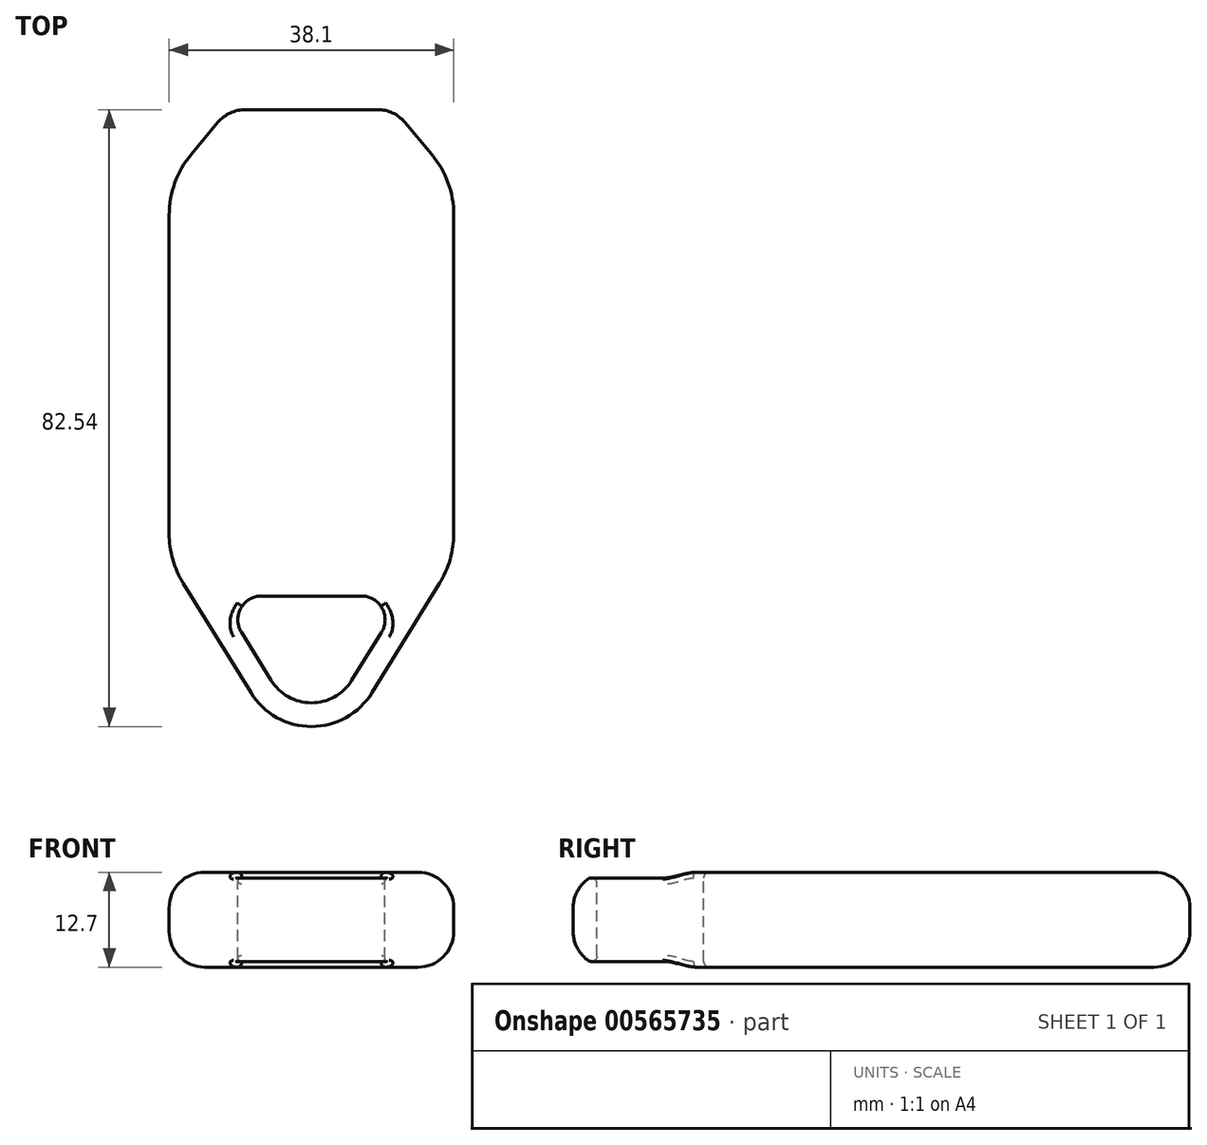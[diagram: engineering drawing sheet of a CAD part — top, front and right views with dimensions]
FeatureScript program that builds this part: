
annotation { "Feature Type Name" : "Feature", "Feature Type Description" : "" }
export const myFeature = defineFeature(function(context is Context, id is Id, definition is map)
    precondition{}
    {
        {
            var Q0;
            Q0=qCreatedBy(makeId("Top.planeOp"),FACE);
            var sketch = newSketch(context, id + "F0", { "sketchPlane" : qUnion([Q0])});
            skLineSegment(sketch, "E0.bottom", {"start": v(19.05, 25.4) * mm, "end": v(-19.05, 25.4) * mm});
            skLineSegment(sketch, "E0.top", {"start": v(19.05, -25.4) * mm, "end": v(-19.05, -25.4) * mm});
            skLineSegment(sketch, "E0.left", {"start": v(19.05, 25.4) * mm, "end": v(19.05, -25.4) * mm});
            skLineSegment(sketch, "E0.right", {"start": v(-19.05, 25.4) * mm, "end": v(-19.05, -25.4) * mm});
            skPoint(sketch, "E0.middle", {"position": v(0, 0) * mm});
            skSolve(sketch);
        }
        {
            var Q0;
            Q0=makeQuery(id+"F0.imprint","IMPRINT",FACE,{"disambiguationData":[TD([[makeQuery(id+"F0.imprint","IMPRINT",EDGE,{"derivedFrom":sQuery(id+"F0.wireOp",EDGE,"E0.bottom")}),1.0]])]});
            extrude(context, id + "F1", {"entities" : qUnion([Q0]), "depth" : 12.7 * mm, "offsetDistance" : 25.4 * mm, "symmetric" : true});
        }
        {
            var Q0;
            Q0=makeQuery(id+"F1.opExtrude","CAP_FACE",FACE,{"disambiguationData":[OSD([sQuery(id+"F0.wireOp",EDGE,"E0.bottom"),sQuery(id+"F0.wireOp",EDGE,"E0.top"),sQuery(id+"F0.wireOp",EDGE,"E0.left"),sQuery(id+"F0.wireOp",EDGE,"E0.right")])],"isStart":false});
            var sketch = newSketch(context, id + "F2", { "sketchPlane" : qUnion([Q0])});
            skLineSegment(sketch, "E1", {"start": v(0, 25.4) * mm, "end": v(0, 34.92) * mm, "construction": true});
            skPoint(sketch, "E1.endSnap0", {"position": v(0, 25.4) * mm});
            skLineSegment(sketch, "E2", {"start": v(-19.05, 25.4) * mm, "end": v(-12.5, 33.22) * mm});
            skLineSegment(sketch, "E3", {"start": v(-8.85, 34.92) * mm, "end": v(0, 34.92) * mm});
            skLineSegment(sketch, "E4.MirrorCS", {"start": v(19.05, 25.4) * mm, "end": v(12.5, 33.22) * mm});
            skLineSegment(sketch, "E5.MirrorCS", {"start": v(8.85, 34.92) * mm, "end": v(0, 34.92) * mm});
            skLineSegment(sketch, "E6", {"start": v(-19.05, 25.4) * mm, "end": v(19.05, 25.4) * mm});
            skLineSegment(sketch, "E7", {"start": v(0, -25.4) * mm, "end": v(0, -38.1) * mm, "construction": true});
            skPoint(sketch, "E7.endSnap0", {"position": v(0, -25.4) * mm});
            skArc(sketch, "E8", {"start": v(-8.1, -43.1) * mm, "mid": v(0, -47.62) * mm, "end": v(8.1, -43.1) * mm});
            skLineSegment(sketch, "E9", {"start": v(-19.05, -25.4) * mm, "end": v(-8.1, -43.1) * mm});
            skLineSegment(sketch, "E10", {"start": v(19.05, -25.4) * mm, "end": v(8.1, -43.1) * mm});
            skArc(sketch, "E11", {"start": v(-5.4, -41.44) * mm, "mid": v(0, -44.45) * mm, "end": v(5.4, -41.44) * mm});
            skLineSegment(sketch, "E12", {"start": v(-5.4, -41.44) * mm, "end": v(-9.38, -35) * mm});
            skLineSegment(sketch, "E13", {"start": v(-6.68, -30.16) * mm, "end": v(6.68, -30.16) * mm});
            skLineSegment(sketch, "E14", {"start": v(9.38, -35) * mm, "end": v(5.4, -41.44) * mm});
            skPoint(sketch, "E15.visualSharp", {"position": v(-12.37, -30.16) * mm});
            skArc(sketch, "E15.filletArc", {"start": v(-6.68, -30.16) * mm, "mid": v(-9.45, -31.8) * mm, "end": v(-9.38, -35) * mm});
            skPoint(sketch, "E16.visualSharp", {"position": v(12.37, -30.16) * mm});
            skArc(sketch, "E16.filletArc", {"start": v(9.38, -35) * mm, "mid": v(9.45, -31.8) * mm, "end": v(6.68, -30.16) * mm});
            skPoint(sketch, "E17.visualSharp", {"position": v(-11.07, 34.93) * mm});
            skArc(sketch, "E17.filletArc", {"start": v(-8.85, 34.93) * mm, "mid": v(-10.86, 34.48) * mm, "end": v(-12.5, 33.22) * mm});
            skPoint(sketch, "E18.visualSharp", {"position": v(11.07, 34.93) * mm});
            skArc(sketch, "E18.filletArc", {"start": v(12.5, 33.22) * mm, "mid": v(10.86, 34.48) * mm, "end": v(8.85, 34.93) * mm});
            skSolve(sketch);
        }
        {
            var Q0;
            Q0=makeQuery(id+"F2.imprint","IMPRINT",FACE,{"disambiguationData":[TD([[makeQuery(id+"F2.imprint","IMPRINT",EDGE,{"derivedFrom":sQuery(id+"F2.wireOp",EDGE,"E2")}),-1.0]])]});
            var Q1;
            Q1=makeQuery(id+"F2.imprint","IMPRINT",FACE,{"disambiguationData":[TD([[makeQuery(id+"F2.imprint","IMPRINT",EDGE,{"derivedFrom":sQuery(id+"F2.wireOp",EDGE,"E8")}),1.0]])]});
            var Q2;
            Q2=makeQuery(id+"F1.opExtrude","CAP_FACE",FACE,{"disambiguationData":[OSD([sQuery(id+"F0.wireOp",EDGE,"E0.bottom"),sQuery(id+"F0.wireOp",EDGE,"E0.top"),sQuery(id+"F0.wireOp",EDGE,"E0.left"),sQuery(id+"F0.wireOp",EDGE,"E0.right")])],"isStart":true});
            extrude(context, id + "F3", {"entities" : qUnion([Q0, Q1]), "operationType" : NewBodyOperationType.ADD, "endBound" : BoundingType.UP_TO_SURFACE, "oppositeDirection" : true, "depth" : 25.4 * mm, "endBoundEntityFace" : qUnion([Q2]), "offsetDistance" : 25.4 * mm});
        }
        {
            var Q0;
            {var subQ0=sQuery(id+"F0.wireOp",EDGE,"E0.right");Q0=makeQuery(id+"F3.boolean.opBoolean","MERGE",EDGE,{"derivedFrom":[makeQuery(id+"F1.opExtrude","SWEPT_EDGE",EDGE,{"disambiguationData":[OSD([sQuery(id+"F0.wireOp",EDGE,"E0.bottom"),subQ0])]}),makeQuery(id+"F3.opExtrude","SWEPT_EDGE",EDGE,{"disambiguationData":[OSD([subQ0,sQuery(id+"F2.wireOp",EDGE,"E2"),sQuery(id+"F2.wireOp",EDGE,"E6")])]})]});}
            var Q1;
            {var subQ0=sQuery(id+"F0.wireOp",EDGE,"E0.left");Q1=makeQuery(id+"F3.boolean.opBoolean","MERGE",EDGE,{"derivedFrom":[makeQuery(id+"F1.opExtrude","SWEPT_EDGE",EDGE,{"disambiguationData":[OSD([sQuery(id+"F0.wireOp",EDGE,"E0.bottom"),subQ0])]}),makeQuery(id+"F3.opExtrude","SWEPT_EDGE",EDGE,{"disambiguationData":[OSD([subQ0,sQuery(id+"F2.wireOp",EDGE,"E4.MirrorCS"),sQuery(id+"F2.wireOp",EDGE,"E6")])]})]});}
            var Q2;
            {var subQ0=sQuery(id+"F0.wireOp",EDGE,"E0.left");var subQ1=sQuery(id+"F0.wireOp",EDGE,"E0.top");Q2=makeQuery(id+"F3.boolean.opBoolean","MERGE",EDGE,{"derivedFrom":[makeQuery(id+"F1.opExtrude","SWEPT_EDGE",EDGE,{"disambiguationData":[OSD([subQ1,subQ0])]}),makeQuery(id+"F3.opExtrude","SWEPT_EDGE",EDGE,{"disambiguationData":[OSD([subQ1,subQ0,sQuery(id+"F2.wireOp",EDGE,"E10")])]})]});}
            var Q3;
            {var subQ0=sQuery(id+"F0.wireOp",EDGE,"E0.right");var subQ1=sQuery(id+"F0.wireOp",EDGE,"E0.top");Q3=makeQuery(id+"F3.boolean.opBoolean","MERGE",EDGE,{"derivedFrom":[makeQuery(id+"F1.opExtrude","SWEPT_EDGE",EDGE,{"disambiguationData":[OSD([subQ1,subQ0])]}),makeQuery(id+"F3.opExtrude","SWEPT_EDGE",EDGE,{"disambiguationData":[OSD([subQ1,subQ0,sQuery(id+"F2.wireOp",EDGE,"E9")])]})]});}
            fillet(context, id + "F4", {"entities" : qUnion([Q0, Q1, Q2, Q3]), "radius" : 12.7 * mm, "tangentPropagation" : true, "allowEdgeOverflow" : false});
        }
        {
            var Q0;
            Q0=makeQuery(id+"F1.opExtrude","CAP_EDGE",EDGE,{"disambiguationData":[OSD([sQuery(id+"F0.wireOp",EDGE,"E0.right")])],"isStart":false});
            var Q1;
            Q1=makeQuery(id+"F1.opExtrude","CAP_EDGE",EDGE,{"disambiguationData":[OSD([sQuery(id+"F0.wireOp",EDGE,"E0.right")])],"isStart":true});
            fillet(context, id + "F5", {"entities" : qUnion([Q0, Q1]), "radius" : 4.76 * mm, "tangentPropagation" : true, "allowEdgeOverflow" : false});
        }
        {
            var Q0;
            Q0=makeQuery(id+"F5.opFillet","BLEND_EDGE",EDGE,{"blendedFrom":[makeQuery(id+"F3.opExtrude","CAP_EDGE",EDGE,{"disambiguationData":[OSD([sQuery(id+"F2.wireOp",EDGE,"E9")])],"isStart":true}),makeQuery(id+"F3.opExtrude","SWEPT_FACE",FACE,{"disambiguationData":[OSD([sQuery(id+"F2.wireOp",EDGE,"E12")])]})],"blendedInto":[makeQuery(id+"F3.opExtrude","SWEPT_FACE",FACE,{"disambiguationData":[OSD([sQuery(id+"F2.wireOp",EDGE,"E12")])]})]});
            var Q1;
            Q1=makeQuery(id+"F5.opFillet","BLEND_EDGE",EDGE,{"blendedFrom":[makeQuery(id+"F3.opExtrude","CAP_EDGE",EDGE,{"disambiguationData":[OSD([sQuery(id+"F2.wireOp",EDGE,"E9")])],"isStart":true}),makeQuery(id+"F3.opExtrude","SWEPT_FACE",FACE,{"disambiguationData":[OSD([sQuery(id+"F2.wireOp",EDGE,"E15.filletArc")])]})],"blendedInto":[makeQuery(id+"F3.opExtrude","SWEPT_FACE",FACE,{"disambiguationData":[OSD([sQuery(id+"F2.wireOp",EDGE,"E15.filletArc")])]})]});
            var Q2;
            Q2=makeQuery(id+"F3.opExtrude","CAP_EDGE",EDGE,{"disambiguationData":[OSD([sQuery(id+"F2.wireOp",EDGE,"E13")])],"isStart":false});
            fillet(context, id + "F6", {"entities" : qUnion([Q0, Q1, Q2]), "radius" : 0.76 * mm, "tangentPropagation" : true, "allowEdgeOverflow" : false});
        }
    });
